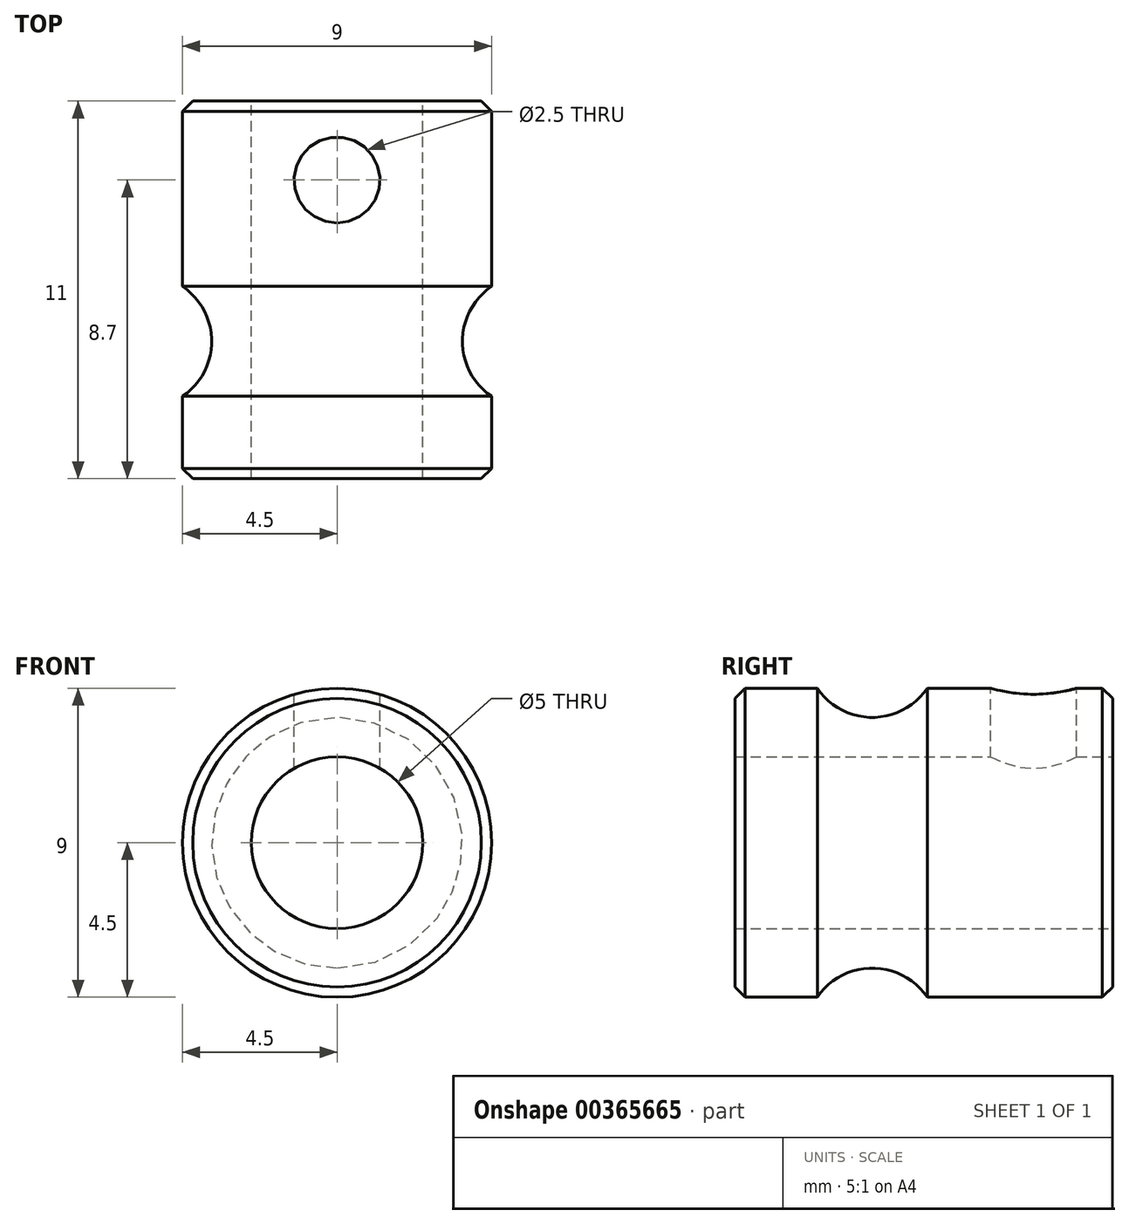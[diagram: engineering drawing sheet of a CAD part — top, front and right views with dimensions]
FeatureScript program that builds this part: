
annotation { "Feature Type Name" : "Feature", "Feature Type Description" : "" }
export const myFeature = defineFeature(function(context is Context, id is Id, definition is map)
    precondition{}
    {
        {
            var Q0;
            Q0=qCreatedBy(makeId("Front.planeOp"),FACE);
            var sketch = newSketch(context, id + "F0", { "sketchPlane" : qUnion([Q0])});
            skCircle(sketch, "E0", {"center": v(0, 0) * mm, "radius": 2.5 * mm});
            skCircle(sketch, "E1", {"center": v(0, 0) * mm, "radius": 4.5 * mm});
            skSolve(sketch);
        }
        {
            var Q0;
            Q0=makeQuery(id+"F0.imprint","IMPRINT",FACE,{"disambiguationData":[TD([[makeQuery(id+"F0.imprint","IMPRINT",EDGE,{"derivedFrom":sQuery(id+"F0.wireOp",EDGE,"E0")}),-1.0]])]});
            extrude(context, id + "F1", {"entities" : qUnion([Q0]), "depth" : 11 * mm, "symmetric" : true});
        }
        {
            var Q0;
            Q0=qCreatedBy(makeId("Right.planeOp"),FACE);
            var sketch = newSketch(context, id + "F2", { "sketchPlane" : qUnion([Q0])});
            skLineSegment(sketch, "E2", {"start": v(5.5, 0) * mm, "end": v(-5.5, 0) * mm, "construction": true});
            skLineSegment(sketch, "E3", {"start": v(-1.5, 0) * mm, "end": v(-1.5, 3.65) * mm, "construction": true});
            skLineSegment(sketch, "E4", {"start": v(3.2, 0) * mm, "end": v(3.2, 4.5) * mm});
            skCircle(sketch, "E5", {"center": v(-1.5, 5.58) * mm, "radius": 1.93 * mm});
            skLineSegment(sketch, "E6", {"start": v(-1.5, 5.58) * mm, "end": v(-1.5, 3.65) * mm, "construction": true});
            skLineSegment(sketch, "E7", {"start": v(-3.1, 4.5) * mm, "end": v(0.1, 4.5) * mm, "construction": true});
            skSolve(sketch);
        }
        {
            var Q0;
            Q0=makeQuery(id+"F2.imprint","IMPRINT",FACE,{"disambiguationData":[TD([[makeQuery(id+"F2.imprint","IMPRINT",EDGE,{"derivedFrom":sQuery(id+"F2.wireOp",EDGE,"E5")}),1.0]])]});
            var Q1;
            Q1=sQuery(id+"F2.wireOp",EDGE,"E2");
            revolve(context, id + "F3", {"operationType" : NewBodyOperationType.REMOVE, "entities" : qUnion([Q0]), "axis" : qUnion([Q1]), "revolveType" : RevolveType.FULL, "oppositeDirection" : true});
        }
        {
            var Q0;
            Q0=sQuery(id+"F2.wireOp",VERTEX,"E4.end");
            var Q1;
            Q1=sQuery(id+"F2.wireOp",EDGE,"E4");
            cPlane(context, id + "F4", {"entities" : qUnion([Q0, Q1]), "cplaneType" : CPlaneType.LINE_POINT, "offset" : 25 * mm, "width" : 150 * mm, "height" : 150 * mm});
        }
        {
            var Q0;
            Q0=qCreatedBy(id+"F4.planeOp",FACE);
            var sketch = newSketch(context, id + "F5", { "sketchPlane" : qUnion([Q0])});
            skPoint(sketch, "E8.0", {"position": v(0, 3.2) * mm});
            skSolve(sketch);
        }
        {
            var Q0;
            Q0=sQuery(id+"F5.wireOp",VERTEX,"E8.0");
            var Q1;
            Q1=makeQuery(id+"F1.opExtrude","SWEPT_BODY",BODY,{"disambiguationData":[OSD([sQuery(id+"F0.wireOp",EDGE,"E0"),sQuery(id+"F0.wireOp",EDGE,"E1")])]});
            hole(context, id + "F6", {"style" : HoleStyle.SIMPLE, "endStyle" : HoleEndStyle.BLIND, "holeDiameter" : 2.5 * mm, "holeDepth" : 4.5 * mm, "locations" : qUnion([Q0]), "scope" : qUnion([Q1])});
        }
        {
            var Q0;
            Q0=makeQuery(id+"F1.opExtrude","CAP_EDGE",EDGE,{"disambiguationData":[OSD([sQuery(id+"F0.wireOp",EDGE,"E1")])],"isStart":false});
            var Q1;
            Q1=makeQuery(id+"F1.opExtrude","CAP_EDGE",EDGE,{"disambiguationData":[OSD([sQuery(id+"F0.wireOp",EDGE,"E1")])],"isStart":true});
            chamfer(context, id + "F7", {"entities" : qUnion([Q0, Q1]), "width" : .3 * mm, "tangentPropagation" : true});
        }
    });
